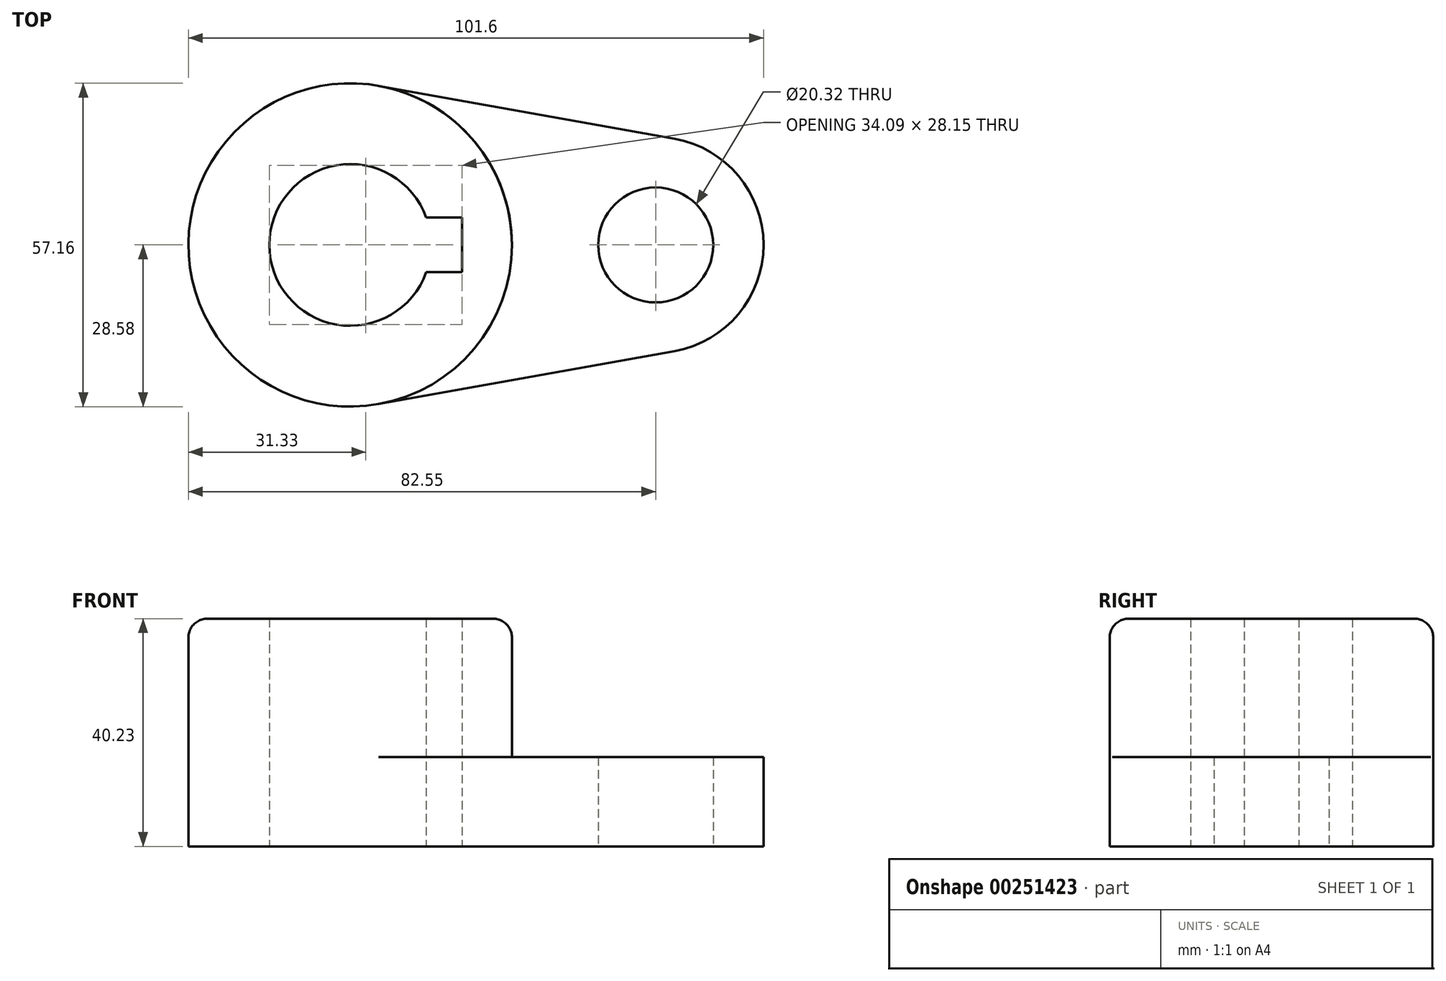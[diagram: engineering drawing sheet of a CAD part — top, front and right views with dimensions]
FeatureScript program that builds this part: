
annotation { "Feature Type Name" : "Feature", "Feature Type Description" : "" }
export const myFeature = defineFeature(function(context is Context, id is Id, definition is map)
    precondition{}
    {
        {
            var Q0;
            Q0=qCreatedBy(makeId("Top.planeOp"),FACE);
            var sketch = newSketch(context, id + "F0", { "sketchPlane" : qUnion([Q0])});
            skArc(sketch, "E0", {"start": v(-40.53, 4.83) * mm, "mid": v(-68.26, 0) * mm, "end": v(-40.53, -4.83) * mm});
            skCircle(sketch, "E1", {"center": v(0, 0) * mm, "radius": 10.16 * mm});
            skCircle(sketch, "E2", {"center": v(-53.97, 0) * mm, "radius": 28.58 * mm});
            skCircle(sketch, "E3", {"center": v(0, 0) * mm, "radius": 19.05 * mm});
            skLineSegment(sketch, "E4.right", {"start": v(-34.18, -4.83) * mm, "end": v(-34.18, 4.83) * mm});
            skLineSegment(sketch, "E5.trimOffspring", {"start": v(-40.53, 4.83) * mm, "end": v(-34.18, 4.83) * mm});
            skLineSegment(sketch, "E6.trimOffspring", {"start": v(-40.53, -4.83) * mm, "end": v(-34.18, -4.83) * mm});
            skLineSegment(sketch, "E7", {"start": v(-53.97, 0) * mm, "end": v(0, 0) * mm, "construction": true});
            skLineSegment(sketch, "E8", {"start": v(-48.93, 28.13) * mm, "end": v(3.36, 18.75) * mm});
            skLineSegment(sketch, "E9", {"start": v(-48.93, -28.13) * mm, "end": v(3.36, -18.75) * mm});
            skSolve(sketch);
        }
        {
            var Q0;
            Q0=makeQuery(id+"F0.imprint","IMPRINT",FACE,{"disambiguationData":[TD([[makeQuery(id+"F0.imprint","IMPRINT",EDGE,{"derivedFrom":sQuery(id+"F0.wireOp",EDGE,"E0")}),-1.0]])]});
            extrude(context, id + "F1", {"entities" : qUnion([Q0]), "depth" : 40.23 * mm});
        }
        {
            var Q0;
            {var subQ0=sQuery(id+"F0.wireOp",EDGE,"o5OdITKO-bEnJ-2VYi-a7Jk-zIUuU5JH3HSI");var subQ1=sQuery(id+"F0.wireOp",EDGE,"E2");var subQ2=makeQuery(id+"F0.imprint","INTERSECT",VERTEX,{"disambiguationData":[OD(1.0)],"derivedFrom":[subQ1,subQ0]});Q0=makeQuery(id+"F0.imprint","IMPRINT",FACE,{"disambiguationData":[TD([[makeQuery(id+"F0.imprint","IMPRINT",EDGE,{"disambiguationData":[TD([[subQ2,1.0]])],"derivedFrom":subQ1}),-1.0]])]});}
            var Q1;
            Q1=makeQuery(id+"F0.imprint","IMPRINT",FACE,{"disambiguationData":[TD([[makeQuery(id+"F0.imprint","IMPRINT",EDGE,{"derivedFrom":sQuery(id+"F0.wireOp",EDGE,"E1")}),-1.0]])]});
            extrude(context, id + "F2", {"entities" : qUnion([Q0, Q1]), "operationType" : NewBodyOperationType.ADD, "depth" : 15.77 * mm});
        }
        {
            var Q0;
            {var subQ0=sQuery(id+"F0.wireOp",EDGE,"E2");Q0=makeQuery(id+"F1.opExtrude","CAP_EDGE",EDGE,{"disambiguationData":[OSD([subQ0]),TDD([makeQuery(id+"F0.imprint","IMPRINT",EDGE,{"disambiguationData":[TD([[makeQuery(id+"F0.imprint","INTERSECT",VERTEX,{"disambiguationData":[OD(0.0)],"derivedFrom":[subQ0,sQuery(id+"F0.wireOp",EDGE,"SRnHb5uK-vhAm-8B8o-SrwD-EHZrL22LgCVp")]}),1.0]])],"derivedFrom":subQ0})])],"isStart":false});}
            var Q1;
            Q1=makeQuery(id+"F1.opExtrude","CAP_EDGE",EDGE,{"disambiguationData":[OSD([sQuery(id+"F0.wireOp",EDGE,"SRnHb5uK-vhAm-8B8o-SrwD-EHZrL22LgCVp")])],"isStart":false});
            var Q2;
            {var subQ0=sQuery(id+"F0.wireOp",EDGE,"E2");Q2=makeQuery(id+"F1.opExtrude","CAP_EDGE",EDGE,{"disambiguationData":[OSD([subQ0]),TDD([makeQuery(id+"F0.imprint","IMPRINT",EDGE,{"disambiguationData":[TD([[makeQuery(id+"F0.imprint","INTERSECT",VERTEX,{"disambiguationData":[OD(1.0)],"derivedFrom":[subQ0,sQuery(id+"F0.wireOp",EDGE,"o5OdITKO-bEnJ-2VYi-a7Jk-zIUuU5JH3HSI")]}),1.0]])],"derivedFrom":subQ0})])],"isStart":false});}
            var Q3;
            Q3=makeQuery(id+"F1.opExtrude","CAP_EDGE",EDGE,{"disambiguationData":[OSD([sQuery(id+"F0.wireOp",EDGE,"o5OdITKO-bEnJ-2VYi-a7Jk-zIUuU5JH3HSI")])],"isStart":false});
            fillet(context, id + "F3", {"entities" : qUnion([Q0, Q1, Q2, Q3]), "radius" : 3.3 * mm, "tangentPropagation" : true, "allowEdgeOverflow" : false});
        }
    });
